# Revit family: Accessory-Cutting_Board-KOHLER-Buckley-K-28905_1
name_source: partatom
category: Specialty Equipment
units: mm (PartAtom-declared; Revit-internal decimal feet)

## family parameters
Cut with Voids When Loaded = No
Host = Face
Maintain Annotation Orientation = No
OmniClass Number = 23.31.13.17
OmniClass Title = Sink Components
Part Type = Normal
Room Calculation Point = No
Round Connector Dimension = Use Diameter
Shared = No

## types (1)
- NA-Natural Bamboo
    ADA Compliant = No
    Assembly Code = C1030200
    Date Modified = 03/06/2022
    Default Elevation = 36"
    Description = BETTER CUTTING BOARD
    Finish = Kohler-Wood-1WS-Bamboo
    Height = 1 3/16"
    Length = 17 5/8"
    Manufacturer = KOHLER Co.
    Master Format 2014 = 10 28 00
    Master Format 2014 Name = Toilet, Bath, and Laundry Accessories
    Material = Bamboo Laminate
    Model = K-28905-NA
    Product Documentation Link = https://www.us.kohler.com
    Product Name = Buckley
    Product Page URL = http://www.us.kohler.com
    Type = 1
    URL = https://www.us.kohler.com
    WaterSense Certified = No
    Width = 11"

## geometry (parser evidence)
native form markers: Sweep x5
no freeform markers — native parametric forms only
